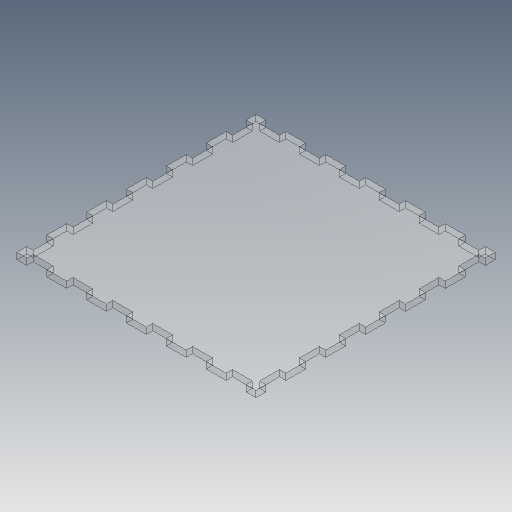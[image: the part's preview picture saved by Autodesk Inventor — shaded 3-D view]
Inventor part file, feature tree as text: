
AUTODESK INVENTOR PART (.ipt)
format: ipt  version: 2018 (Build 220112000, 112)  size: 216,576 bytes
history: native  units: in
note: dims shown in document units (in); Inventor stores cm internally (conversion verified against a paired STEP export)
features: extrude x3, sketch x3, pattern_linear x2, mirror x2, projected_geometry x2
ambient origin geometry x8: Origin, YZ Plane, XZ Plane, XY Plane, X Axis, Y Axis, Z Axis, Center Point
bodies: Solid1 (feature_tree)
feature tree (12):
  extrude  "Extrusion1"  Depth=4.7244in
  extrude  "Extrusion3"  TaperAngle=0.0deg  [1 undecoded]
  pattern_linear  "Rectangular Pattern2"  Spacing1=0.1969in  [1 undecoded]
  mirror  "Mirror2"
  extrude  "Extrusion4"  Depth=0.3937in TaperAngle=0.0deg
  pattern_linear  "Rectangular Pattern3"  Count1=6  [1 undecoded]
  mirror  "Mirror3"
  sketch  "Sketch1"  dims[d0=4.7244in d1=4.7244in]
  sketch  "Sketch5"  dims[d2=0.125in d3=0.0in]
  projected_geometry  "Projected Loop4"
  sketch  "Sketch6"  dims[d25=0.3937in d27=0.1969in d28=0.3937in d29=0.0in d30=2.3622in d32=0.7874in d34=0.3937in d35=0.1969in d36=0.3937in d37=0.0in d38=2.3622in d40=0.7874in d41=0.125in d42=0.125in]
  projected_geometry  "Projected Loop5"
note: 3 required parameter values undecoded (feature->parameter linkage not recoverable at this tier; creation-order binding heuristic only, values carry confidence <= 0.55)
